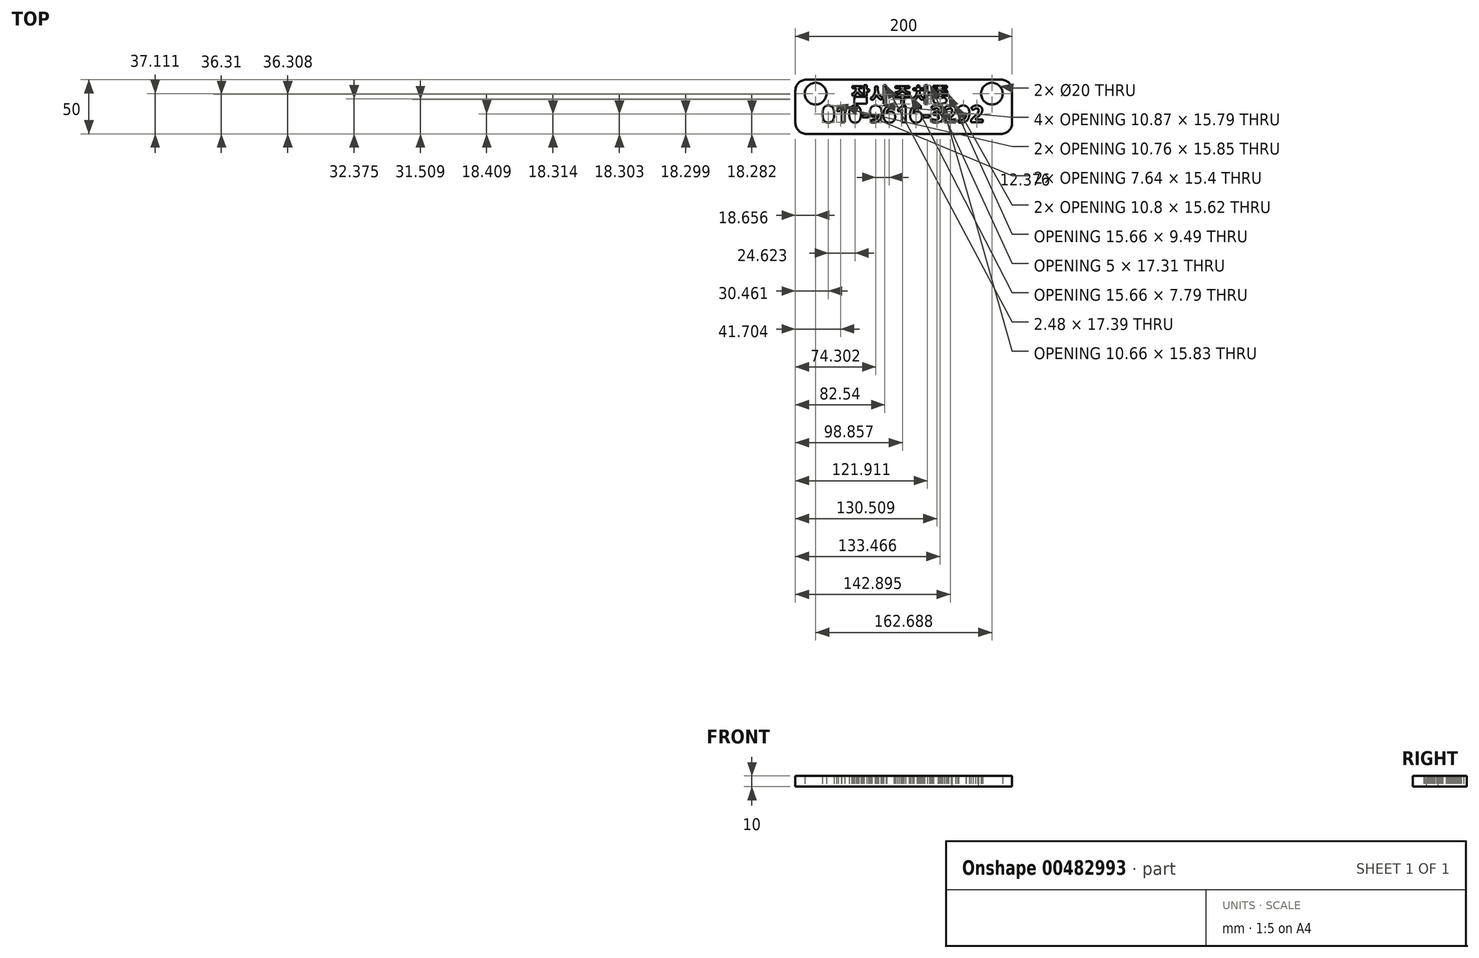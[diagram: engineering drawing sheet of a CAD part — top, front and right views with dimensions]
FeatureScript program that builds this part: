
annotation { "Feature Type Name" : "Feature", "Feature Type Description" : "" }
export const myFeature = defineFeature(function(context is Context, id is Id, definition is map)
    precondition{}
    {
        {
            var Q0;
            Q0=qCreatedBy(makeId("Top.planeOp"),FACE);
            var sketch = newSketch(context, id + "F0", { "sketchPlane" : qUnion([Q0])});
            skLineSegment(sketch, "E0", {"start": v(0, 7.18) * mm, "end": v(90, 7.18) * mm});
            skLineSegment(sketch, "E1", {"start": v(0, 7.18) * mm, "end": v(-90, 7.18) * mm});
            skLineSegment(sketch, "E2", {"start": v(-100, -2.82) * mm, "end": v(-100, -32.82) * mm});
            skLineSegment(sketch, "E3", {"start": v(-90, -42.82) * mm, "end": v(90, -42.82) * mm});
            skLineSegment(sketch, "E4", {"start": v(100, -32.82) * mm, "end": v(100, -2.82) * mm});
            skPoint(sketch, "E5.visualSharp", {"position": v(-100, 7.18) * mm});
            skArc(sketch, "E5.filletArc", {"start": v(-90, 7.18) * mm, "mid": v(-97.07, 4.25) * mm, "end": v(-100, -2.82) * mm});
            skPoint(sketch, "E6.visualSharp", {"position": v(100, 7.18) * mm});
            skArc(sketch, "E6.filletArc", {"start": v(100, -2.82) * mm, "mid": v(97.07, 4.25) * mm, "end": v(90, 7.18) * mm});
            skPoint(sketch, "E7.visualSharp", {"position": v(100, -42.82) * mm});
            skArc(sketch, "E7.filletArc", {"start": v(90, -42.82) * mm, "mid": v(97.07, -39.89) * mm, "end": v(100, -32.82) * mm});
            skPoint(sketch, "E8.visualSharp", {"position": v(-100, -42.82) * mm});
            skArc(sketch, "E8.filletArc", {"start": v(-100, -32.82) * mm, "mid": v(-97.07, -39.89) * mm, "end": v(-90, -42.82) * mm});
            skCircle(sketch, "E9", {"center": v(-81.34, -5.7) * mm, "radius": 10 * mm});
            skCircle(sketch, "E10.MirrorC", {"center": v(81.34, -5.7) * mm, "radius": 10 * mm});
            skText(sketch, "E11", { "text": "010-9616-3292\n", "fontName": "OpenSans-Bold.ttf"});
            skText(sketch, "E12", { "text": "잠시 주차중", "fontName": "NotoSansCJKkr-Bold.otf"});
            const initialGuessF0  = {"E11": [-0.0757, -0.03222, 1, 0, 0.01553], "E12": [-0.0487, -0.01355, 1, 0, 0.01355]};
            skSetInitialGuess(sketch, initialGuessF0);
            skSolve(sketch);
        }
        {
            var Q0;
            Q0 = qSketchRegion(id + "F0", true);
            extrude(context, id + "F1", {"entities" : qUnion([Q0]), "depth" : 10 * mm});
        }
    });
